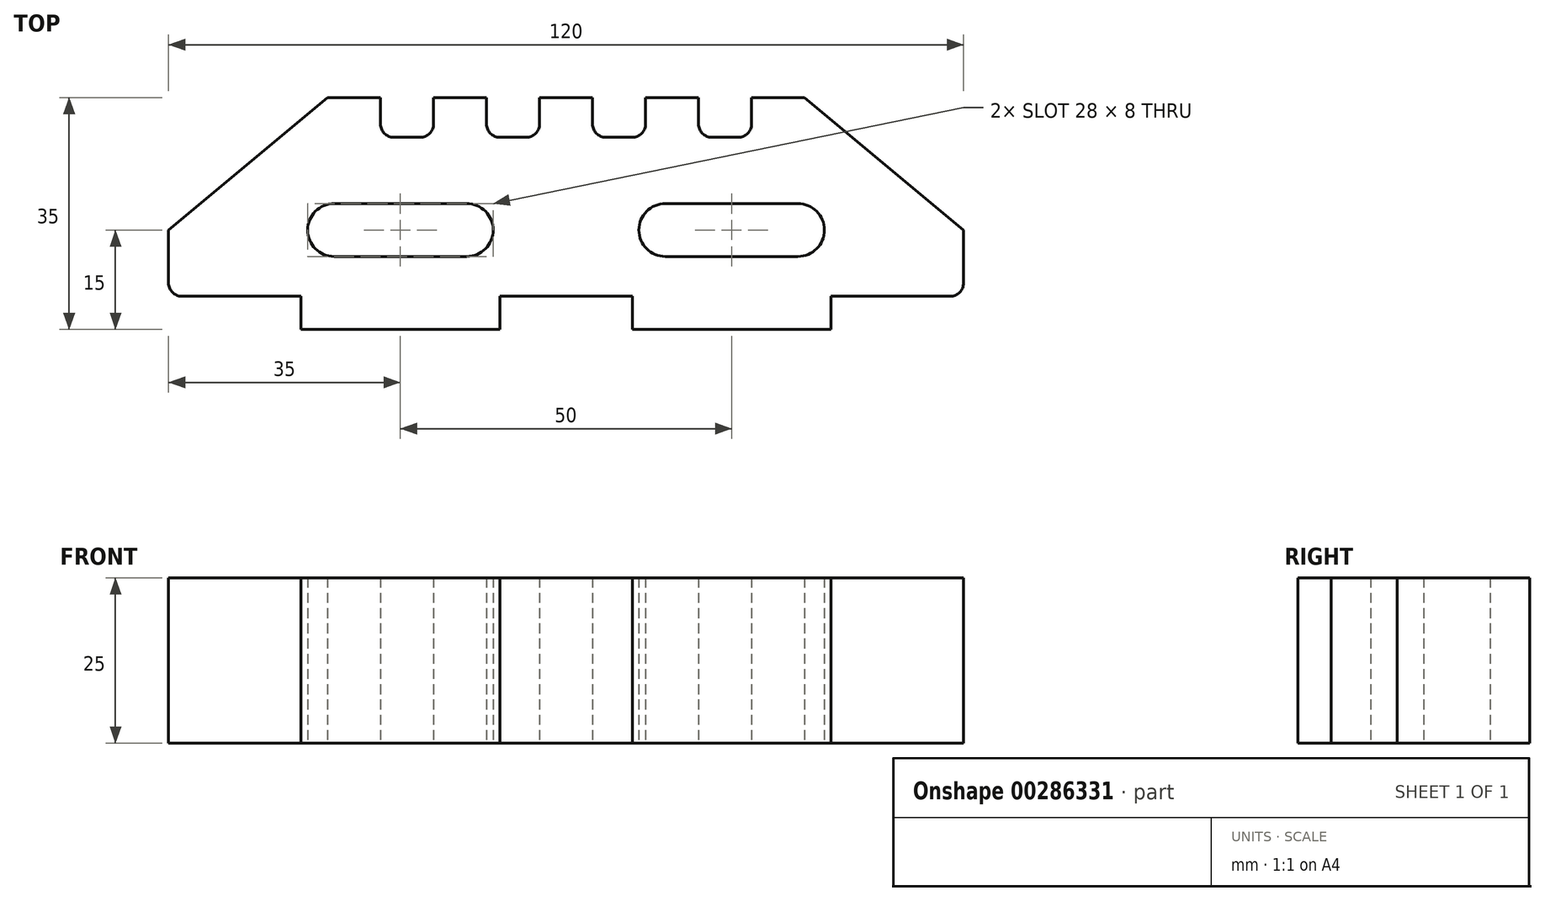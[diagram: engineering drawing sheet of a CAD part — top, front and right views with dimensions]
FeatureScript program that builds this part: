
annotation { "Feature Type Name" : "Feature", "Feature Type Description" : "" }
export const myFeature = defineFeature(function(context is Context, id is Id, definition is map)
    precondition{}
    {
        {
            var Q0;
            Q0=qCreatedBy(makeId("Top.planeOp"),FACE);
            var sketch = newSketch(context, id + "F0", { "sketchPlane" : qUnion([Q0])});
            skLineSegment(sketch, "E0", {"start": v(2, 0) * mm, "end": v(20, 0) * mm});
            skLineSegment(sketch, "E1", {"start": v(20, 0) * mm, "end": v(20, -5) * mm});
            skLineSegment(sketch, "E2", {"start": v(20, -5) * mm, "end": v(50, -5) * mm});
            skLineSegment(sketch, "E3", {"start": v(50, -5) * mm, "end": v(50, 0) * mm});
            skLineSegment(sketch, "E4", {"start": v(50, 0) * mm, "end": v(70, 0) * mm});
            skLineSegment(sketch, "E5", {"start": v(70, 0) * mm, "end": v(70, -5) * mm});
            skLineSegment(sketch, "E6", {"start": v(70, -5) * mm, "end": v(100, -5) * mm});
            skLineSegment(sketch, "E7", {"start": v(100, -5) * mm, "end": v(100, 0) * mm});
            skLineSegment(sketch, "E8", {"start": v(100, 0) * mm, "end": v(118, 0) * mm});
            skLineSegment(sketch, "E9", {"start": v(120, 2) * mm, "end": v(120, 10) * mm});
            skLineSegment(sketch, "E10", {"start": v(0, 2) * mm, "end": v(0, 10) * mm});
            skLineSegment(sketch, "E11", {"start": v(0, 10) * mm, "end": v(24, 30) * mm});
            skLineSegment(sketch, "E12", {"start": v(24, 30) * mm, "end": v(32, 30) * mm});
            skLineSegment(sketch, "E13", {"start": v(32, 30) * mm, "end": v(32, 26) * mm});
            skLineSegment(sketch, "E14", {"start": v(34, 24) * mm, "end": v(38, 24) * mm});
            skLineSegment(sketch, "E15", {"start": v(40, 26) * mm, "end": v(40, 30) * mm});
            skLineSegment(sketch, "E16", {"start": v(40, 30) * mm, "end": v(48, 30) * mm});
            skLineSegment(sketch, "E17", {"start": v(48, 30) * mm, "end": v(48, 26) * mm});
            skLineSegment(sketch, "E18", {"start": v(50, 24) * mm, "end": v(54, 24) * mm});
            skLineSegment(sketch, "E19", {"start": v(56, 26) * mm, "end": v(56, 30) * mm});
            skLineSegment(sketch, "E20", {"start": v(56, 30) * mm, "end": v(64, 30) * mm});
            skLineSegment(sketch, "E21", {"start": v(64, 30) * mm, "end": v(64, 26) * mm});
            skLineSegment(sketch, "E22", {"start": v(66, 24) * mm, "end": v(70, 24) * mm});
            skLineSegment(sketch, "E23", {"start": v(72, 26) * mm, "end": v(72, 30) * mm});
            skLineSegment(sketch, "E24", {"start": v(72, 30) * mm, "end": v(80, 30) * mm});
            skLineSegment(sketch, "E25", {"start": v(80, 30) * mm, "end": v(80, 26) * mm});
            skLineSegment(sketch, "E26", {"start": v(82, 24) * mm, "end": v(86, 24) * mm});
            skLineSegment(sketch, "E27", {"start": v(88, 26) * mm, "end": v(88, 30) * mm});
            skLineSegment(sketch, "E28", {"start": v(88, 30) * mm, "end": v(96, 30) * mm});
            skLineSegment(sketch, "E29", {"start": v(96, 30) * mm, "end": v(120, 10) * mm});
            skLineSegment(sketch, "E30", {"start": v(60, 30) * mm, "end": v(60, 0) * mm, "construction": true});
            skLineSegment(sketch, "E31", {"start": v(75, 6) * mm, "end": v(95, 6) * mm});
            skLineSegment(sketch, "E32", {"start": v(99, 10) * mm, "end": v(99, 10) * mm});
            skLineSegment(sketch, "E33", {"start": v(95, 14) * mm, "end": v(75, 14) * mm});
            skLineSegment(sketch, "E34", {"start": v(71, 10) * mm, "end": v(71, 10) * mm});
            skLineSegment(sketch, "E35", {"start": v(71, 10) * mm, "end": v(99, 10) * mm, "construction": true});
            skLineSegment(sketch, "E36", {"start": v(25, 14) * mm, "end": v(45, 14) * mm});
            skLineSegment(sketch, "E37", {"start": v(49, 10) * mm, "end": v(49, 10) * mm});
            skLineSegment(sketch, "E38", {"start": v(45, 6) * mm, "end": v(25, 6) * mm});
            skLineSegment(sketch, "E39", {"start": v(21, 10) * mm, "end": v(21, 10) * mm});
            skLineSegment(sketch, "E40", {"start": v(21, 10) * mm, "end": v(49, 10) * mm, "construction": true});
            skPoint(sketch, "E41.visualSharp", {"position": v(32, 24) * mm});
            skArc(sketch, "E41.filletArc", {"start": v(32, 26) * mm, "mid": v(32.59, 24.59) * mm, "end": v(34, 24) * mm});
            skPoint(sketch, "E42.visualSharp", {"position": v(40, 24) * mm});
            skArc(sketch, "E42.filletArc", {"start": v(38, 24) * mm, "mid": v(39.41, 24.59) * mm, "end": v(40, 26) * mm});
            skPoint(sketch, "E43.visualSharp", {"position": v(48, 24) * mm});
            skArc(sketch, "E43.filletArc", {"start": v(48, 26) * mm, "mid": v(48.59, 24.59) * mm, "end": v(50, 24) * mm});
            skPoint(sketch, "E44.visualSharp", {"position": v(56, 24) * mm});
            skArc(sketch, "E44.filletArc", {"start": v(54, 24) * mm, "mid": v(55.41, 24.59) * mm, "end": v(56, 26) * mm});
            skPoint(sketch, "E45.visualSharp", {"position": v(64, 24) * mm});
            skArc(sketch, "E45.filletArc", {"start": v(64, 26) * mm, "mid": v(64.59, 24.59) * mm, "end": v(66, 24) * mm});
            skPoint(sketch, "E46.visualSharp", {"position": v(72, 24) * mm});
            skArc(sketch, "E46.filletArc", {"start": v(70, 24) * mm, "mid": v(71.41, 24.59) * mm, "end": v(72, 26) * mm});
            skPoint(sketch, "E47.visualSharp", {"position": v(80, 24) * mm});
            skArc(sketch, "E47.filletArc", {"start": v(80, 26) * mm, "mid": v(80.59, 24.59) * mm, "end": v(82, 24) * mm});
            skPoint(sketch, "E48.visualSharp", {"position": v(88, 24) * mm});
            skArc(sketch, "E48.filletArc", {"start": v(86, 24) * mm, "mid": v(87.41, 24.59) * mm, "end": v(88, 26) * mm});
            skPoint(sketch, "E49.visualSharp", {"position": v(21, 14) * mm});
            skArc(sketch, "E49.filletArc", {"start": v(25, 14) * mm, "mid": v(22.17, 12.83) * mm, "end": v(21, 10) * mm});
            skPoint(sketch, "E50.visualSharp", {"position": v(21, 6) * mm});
            skArc(sketch, "E50.filletArc", {"start": v(21, 10) * mm, "mid": v(22.17, 7.17) * mm, "end": v(25, 6) * mm});
            skPoint(sketch, "E51.visualSharp", {"position": v(49, 6) * mm});
            skArc(sketch, "E51.filletArc", {"start": v(45, 6) * mm, "mid": v(47.83, 7.17) * mm, "end": v(49, 10) * mm});
            skPoint(sketch, "E52.visualSharp", {"position": v(49, 14) * mm});
            skArc(sketch, "E52.filletArc", {"start": v(49, 10) * mm, "mid": v(47.83, 12.83) * mm, "end": v(45, 14) * mm});
            skPoint(sketch, "E53.visualSharp", {"position": v(71, 14) * mm});
            skArc(sketch, "E53.filletArc", {"start": v(75, 14) * mm, "mid": v(72.17, 12.83) * mm, "end": v(71, 10) * mm});
            skPoint(sketch, "E54.visualSharp", {"position": v(99, 14) * mm});
            skArc(sketch, "E54.filletArc", {"start": v(99, 10) * mm, "mid": v(97.83, 12.83) * mm, "end": v(95, 14) * mm});
            skPoint(sketch, "E55.visualSharp", {"position": v(99, 6) * mm});
            skArc(sketch, "E55.filletArc", {"start": v(95, 6) * mm, "mid": v(97.83, 7.17) * mm, "end": v(99, 10) * mm});
            skPoint(sketch, "E56.visualSharp", {"position": v(71, 6) * mm});
            skArc(sketch, "E56.filletArc", {"start": v(71, 10) * mm, "mid": v(72.17, 7.17) * mm, "end": v(75, 6) * mm});
            skPoint(sketch, "E57.visualSharp", {"position": v(0, 0) * mm});
            skArc(sketch, "E57.filletArc", {"start": v(0, 2) * mm, "mid": v(0.59, 0.59) * mm, "end": v(2, 0) * mm});
            skPoint(sketch, "E58.visualSharp", {"position": v(120, 0) * mm});
            skArc(sketch, "E58.filletArc", {"start": v(118, 0) * mm, "mid": v(119.41, 0.59) * mm, "end": v(120, 2) * mm});
            skSolve(sketch);
        }
        {
            var Q0;
            Q0 = qSketchRegion(id + "F0", true);
            extrude(context, id + "F1", {"entities" : qUnion([Q0]), "depth" : 25 * mm});
        }
    });
